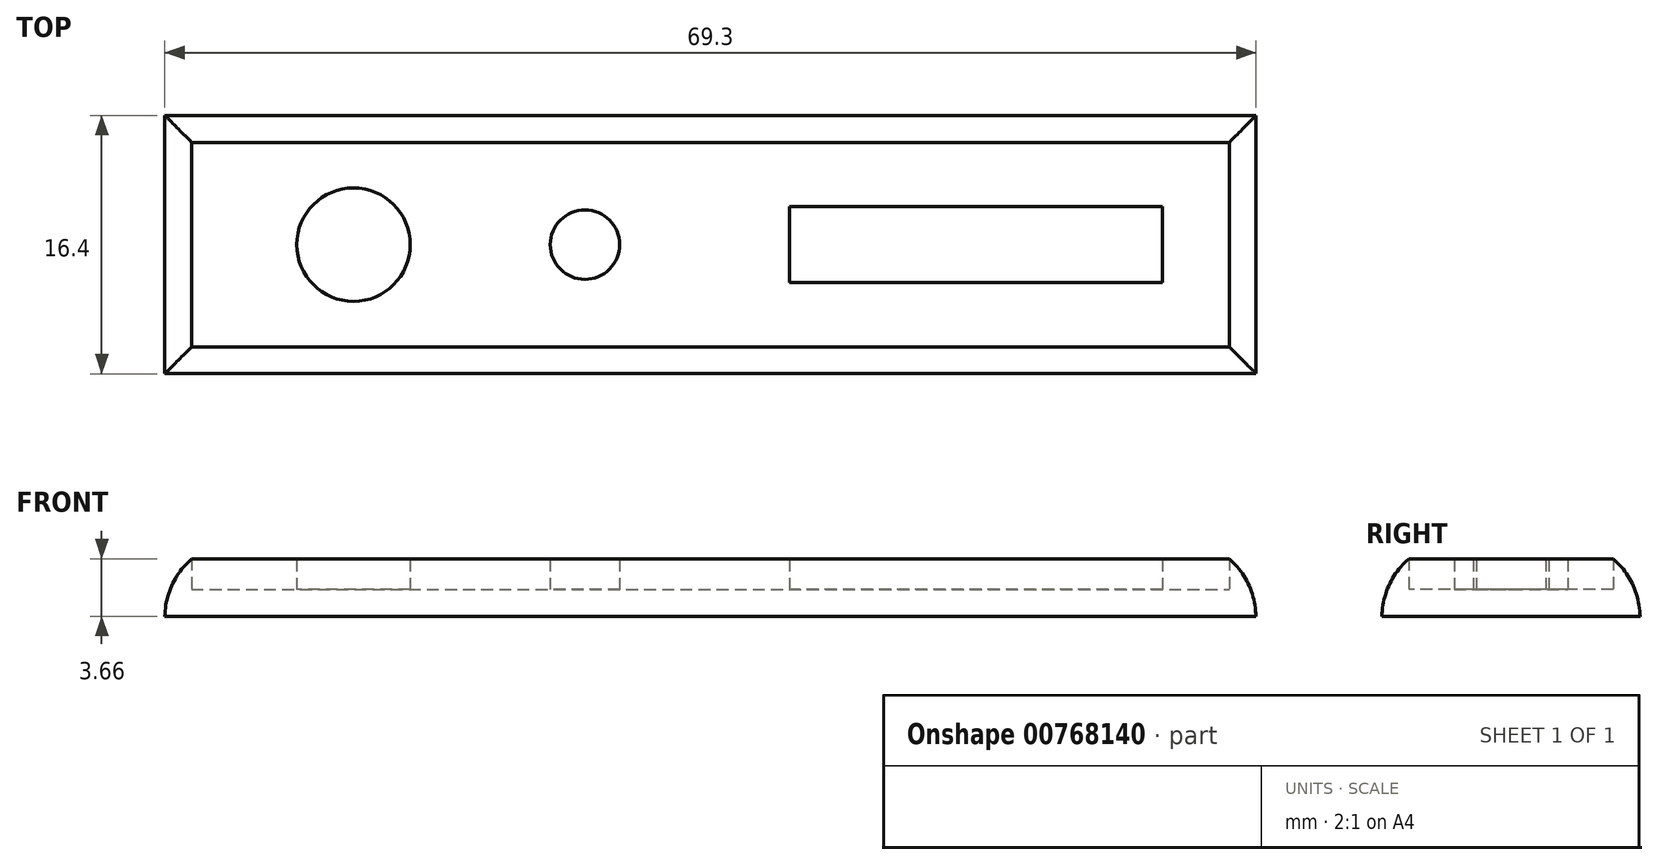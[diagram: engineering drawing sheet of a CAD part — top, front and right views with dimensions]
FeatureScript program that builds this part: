
annotation { "Feature Type Name" : "Feature", "Feature Type Description" : "" }
export const myFeature = defineFeature(function(context is Context, id is Id, definition is map)
    precondition{}
    {
        {
            var Q0;
            Q0=qCreatedBy(makeId("Top.planeOp"),FACE);
            var sketch = newSketch(context, id + "F0", { "sketchPlane" : qUnion([Q0])});
            skLineSegment(sketch, "E0.bottom", {"start": v(-34.65, 8.2) * mm, "end": v(34.65, 8.2) * mm});
            skLineSegment(sketch, "E0.top", {"start": v(-34.65, -8.2) * mm, "end": v(34.65, -8.2) * mm});
            skLineSegment(sketch, "E0.left", {"start": v(-34.65, 8.2) * mm, "end": v(-34.65, -8.2) * mm});
            skLineSegment(sketch, "E0.right", {"start": v(34.65, 8.2) * mm, "end": v(34.65, -8.2) * mm});
            skPoint(sketch, "E0.middle", {"position": v(0, 0) * mm});
            skSolve(sketch);
        }
        {
            var Q0;
            Q0 = qSketchRegion(id + "F0", true);
            extrude(context, id + "F1", {"entities" : qUnion([Q0]), "depth" : 4.9 * mm, "offsetDistance" : 25 * mm});
        }
        {
            var Q0;
            Q0=makeQuery(id+"F1.opExtrude","CAP_FACE",FACE,{"disambiguationData":[OSD([sQuery(id+"F0.wireOp",EDGE,"E0.bottom"),sQuery(id+"F0.wireOp",EDGE,"E0.top"),sQuery(id+"F0.wireOp",EDGE,"E0.left"),sQuery(id+"F0.wireOp",EDGE,"E0.right")])],"isStart":false});
            shell(context, id + "F2", {"entities" : qUnion([Q0]), "thickness" : 1.7 * mm});
        }
        {
            var Q0;
            Q0=makeQuery(id+"F1.opExtrude","CAP_EDGE",EDGE,{"disambiguationData":[OSD([sQuery(id+"F0.wireOp",EDGE,"E0.top")])],"isStart":false});
            var Q1;
            Q1=makeQuery(id+"F1.opExtrude","CAP_EDGE",EDGE,{"disambiguationData":[OSD([sQuery(id+"F0.wireOp",EDGE,"E0.right")])],"isStart":false});
            var Q2;
            Q2=makeQuery(id+"F1.opExtrude","CAP_EDGE",EDGE,{"disambiguationData":[OSD([sQuery(id+"F0.wireOp",EDGE,"E0.bottom")])],"isStart":false});
            var Q3;
            Q3=makeQuery(id+"F1.opExtrude","CAP_EDGE",EDGE,{"disambiguationData":[OSD([sQuery(id+"F0.wireOp",EDGE,"E0.left")])],"isStart":false});
            fillet(context, id + "F3", {"entities" : qUnion([Q0, Q1, Q2, Q3]), "radius" : 5 * mm, "tangentPropagation" : true, "allowEdgeOverflow" : false});
        }
        {
            var Q0;
            Q0=makeQuery(id+"F2.opShell","OFFSET_FACE",FACE,{"disambiguationData":[OSD([sQuery(id+"F0.wireOp",EDGE,"E0.bottom"),sQuery(id+"F0.wireOp",EDGE,"E0.top"),sQuery(id+"F0.wireOp",EDGE,"E0.left"),sQuery(id+"F0.wireOp",EDGE,"E0.right")])]});
            var sketch = newSketch(context, id + "F4", { "sketchPlane" : qUnion([Q0])});
            skCircle(sketch, "E1", {"center": v(-22.67, 0) * mm, "radius": 3.6 * mm});
            skSolve(sketch);
        }
        {
            var Q0;
            Q0 = qSketchRegion(id + "F4", true);
            extrude(context, id + "F5", {"entities" : qUnion([Q0]), "operationType" : NewBodyOperationType.ADD, "depth" : 1.9 * mm, "offsetDistance" : 25 * mm});
        }
        {
            var Q0;
            Q0=makeQuery(id+"F2.opShell","OFFSET_FACE",FACE,{"disambiguationData":[OSD([sQuery(id+"F0.wireOp",EDGE,"E0.bottom"),sQuery(id+"F0.wireOp",EDGE,"E0.top"),sQuery(id+"F0.wireOp",EDGE,"E0.left"),sQuery(id+"F0.wireOp",EDGE,"E0.right")])]});
            var sketch = newSketch(context, id + "F6", { "sketchPlane" : qUnion([Q0])});
            skLineSegment(sketch, "E2.bottom", {"start": v(28.7, 2.4) * mm, "end": v(5.02, 2.4) * mm});
            skLineSegment(sketch, "E2.top", {"start": v(28.7, -2.4) * mm, "end": v(5.02, -2.4) * mm});
            skLineSegment(sketch, "E2.left", {"start": v(28.7, 2.4) * mm, "end": v(28.7, -2.4) * mm});
            skLineSegment(sketch, "E2.right", {"start": v(5.02, 2.4) * mm, "end": v(5.02, -2.4) * mm});
            skPoint(sketch, "E2.middle", {"position": v(16.86, 0) * mm});
            skSolve(sketch);
        }
        {
            var Q0;
            Q0 = qSketchRegion(id + "F6", true);
            extrude(context, id + "F7", {"entities" : qUnion([Q0]), "operationType" : NewBodyOperationType.ADD, "depth" : 1.9 * mm, "offsetDistance" : 25 * mm});
        }
        {
            var Q0;
            Q0=makeQuery(id+"F2.opShell","OFFSET_FACE",FACE,{"disambiguationData":[OSD([sQuery(id+"F0.wireOp",EDGE,"E0.bottom"),sQuery(id+"F0.wireOp",EDGE,"E0.top"),sQuery(id+"F0.wireOp",EDGE,"E0.left"),sQuery(id+"F0.wireOp",EDGE,"E0.right")])]});
            var sketch = newSketch(context, id + "F8", { "sketchPlane" : qUnion([Q0])});
            skCircle(sketch, "E3", {"center": v(-7.97, 0) * mm, "radius": 2.2 * mm});
            skSolve(sketch);
        }
        {
            var Q0;
            Q0 = qSketchRegion(id + "F8", true);
            extrude(context, id + "F9", {"entities" : qUnion([Q0]), "operationType" : NewBodyOperationType.ADD, "depth" : 1.9 * mm, "offsetDistance" : 25 * mm});
        }
    });
